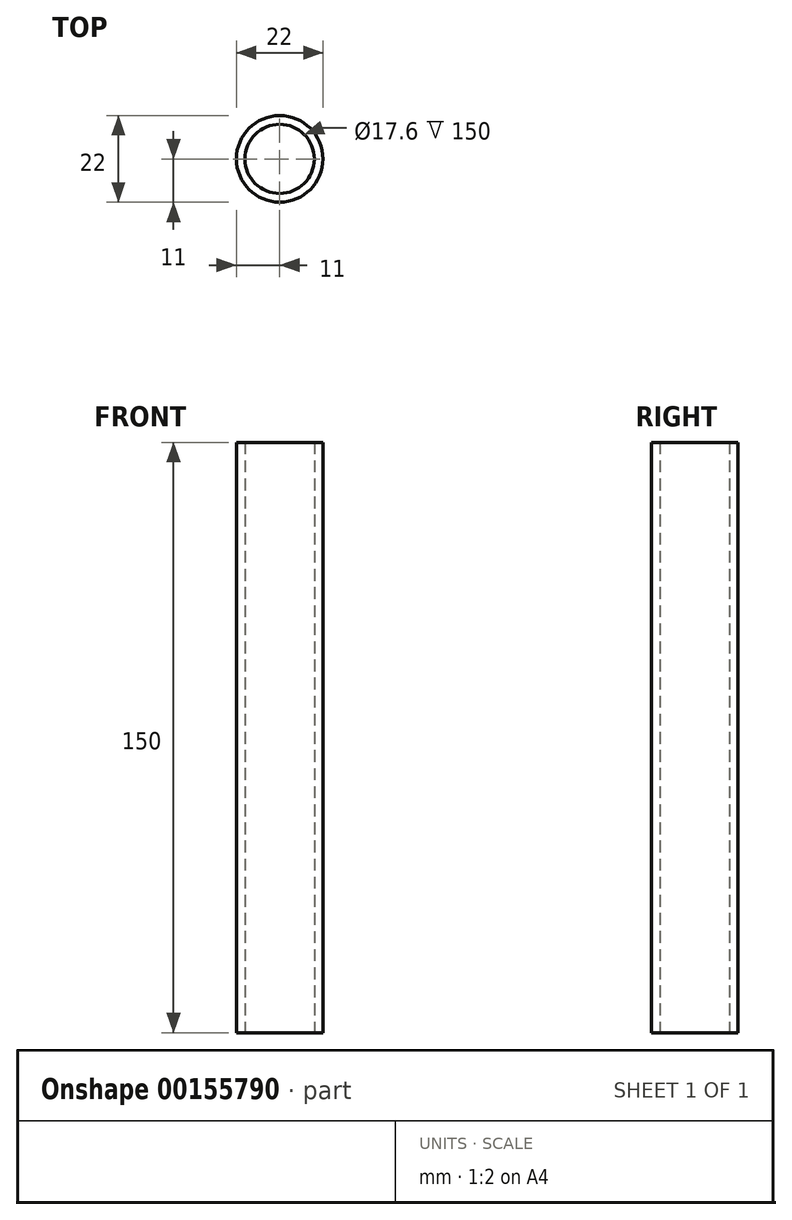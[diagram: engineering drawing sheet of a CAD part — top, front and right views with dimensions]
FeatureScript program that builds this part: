
annotation { "Feature Type Name" : "Feature", "Feature Type Description" : "" }
export const myFeature = defineFeature(function(context is Context, id is Id, definition is map)
    precondition{}
    {
        {
            var Q0;
            Q0=qCreatedBy(makeId("Top.planeOp"),FACE);
            var sketch = newSketch(context, id + "F0", { "sketchPlane" : qUnion([Q0])});
            skCircle(sketch, "E0", {"center": v(0, 0) * mm, "radius": 11 * mm});
            skCircle(sketch, "E1", {"center": v(0, 0) * mm, "radius": 8.8 * mm});
            skSolve(sketch);
        }
        {
            var Q0;
            Q0 = qSketchRegion(id + "F0", true);
            extrude(context, id + "F1", {"entities" : qUnion([Q0]), "depth" : 150 * mm});
        }
    });
